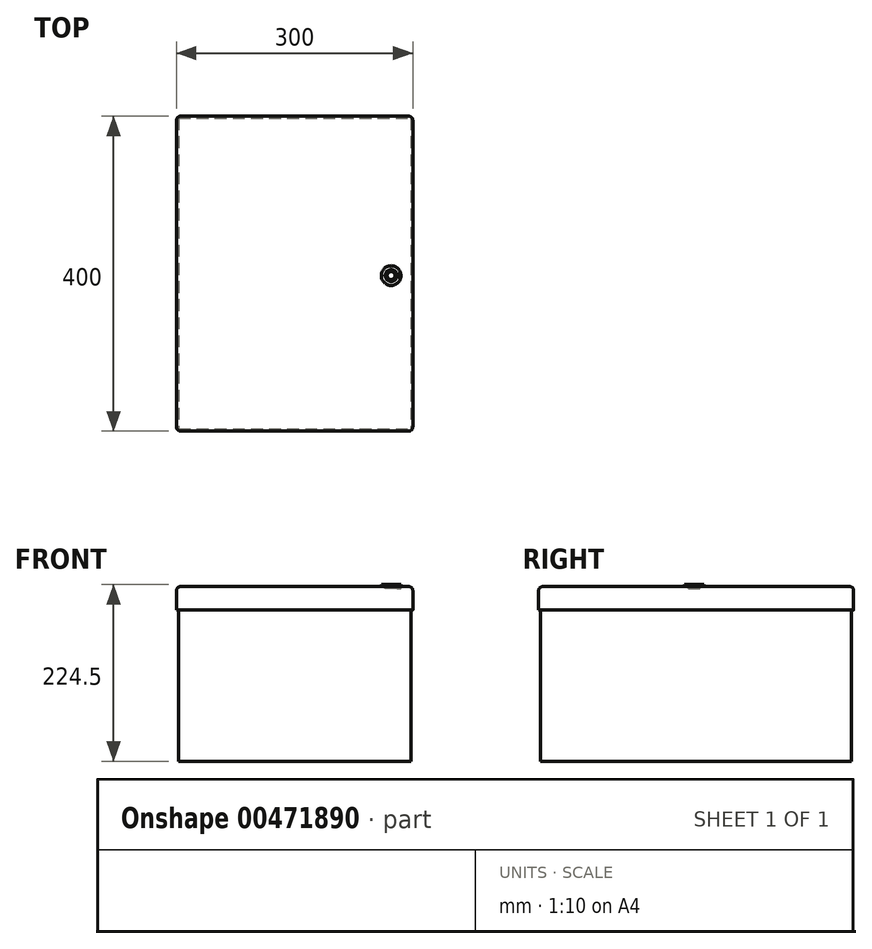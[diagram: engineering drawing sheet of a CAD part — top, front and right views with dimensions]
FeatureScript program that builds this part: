
annotation { "Feature Type Name" : "Feature", "Feature Type Description" : "" }
export const myFeature = defineFeature(function(context is Context, id is Id, definition is map)
    precondition{}
    {
        {
            var Q0;
            Q0=qCreatedBy(makeId("Top.planeOp"),FACE);
            var sketch = newSketch(context, id + "F0", { "sketchPlane" : qUnion([Q0])});
            skLineSegment(sketch, "E0.bottom", {"start": v(-145, 200) * mm, "end": v(150, 200) * mm});
            skLineSegment(sketch, "E0.top", {"start": v(-145, -195) * mm, "end": v(150, -195) * mm});
            skLineSegment(sketch, "E0.left", {"start": v(-145, 200) * mm, "end": v(-145, -195) * mm});
            skLineSegment(sketch, "E0.right", {"start": v(150, 200) * mm, "end": v(150, -195) * mm});
            skSolve(sketch);
        }
        {
            var Q0;
            Q0=makeQuery(id+"F0.imprint","IMPRINT",FACE,{"disambiguationData":[TD([[makeQuery(id+"F0.imprint","IMPRINT",EDGE,{"derivedFrom":sQuery(id+"F0.wireOp",EDGE,"E0.bottom")}),-1.0]])]});
            extrude(context, id + "F1", {"entities" : qUnion([Q0]), "endBound" : BoundingType.SYMMETRIC, "depth" : 220 * mm});
        }
        {
            var Q0;
            Q0=makeQuery(id+"F1.opExtrude","CAP_FACE",FACE,{"disambiguationData":[OSD([sQuery(id+"F0.wireOp",EDGE,"E0.bottom"),sQuery(id+"F0.wireOp",EDGE,"E0.top"),sQuery(id+"F0.wireOp",EDGE,"E0.left"),sQuery(id+"F0.wireOp",EDGE,"E0.right")])],"isStart":false});
            cPlane(context, id + "F2", {"entities" : qUnion([Q0]), "cplaneType" : CPlaneType.OFFSET, "offset" : 2 * mm, "width" : 150 * mm, "height" : 150 * mm});
        }
        {
            var Q0;
            Q0=qCreatedBy(id+"F2.planeOp",FACE);
            var sketch = newSketch(context, id + "F3", { "sketchPlane" : qUnion([Q0])});
            skLineSegment(sketch, "E1.bottom", {"start": v(-147.5, 202.5) * mm, "end": v(152.5, 202.5) * mm});
            skLineSegment(sketch, "E1.top", {"start": v(-147.5, -197.5) * mm, "end": v(152.5, -197.5) * mm});
            skLineSegment(sketch, "E1.left", {"start": v(-147.5, 202.5) * mm, "end": v(-147.5, -197.5) * mm});
            skLineSegment(sketch, "E1.right", {"start": v(152.5, 202.5) * mm, "end": v(152.5, -197.5) * mm});
            skSolve(sketch);
        }
        {
            var Q0;
            Q0=makeQuery(id+"F3.imprint","IMPRINT",FACE,{"disambiguationData":[TD([[makeQuery(id+"F3.imprint","IMPRINT",EDGE,{"derivedFrom":sQuery(id+"F3.wireOp",EDGE,"E1.bottom")}),-1.0]])]});
            extrude(context, id + "F4", {"entities" : qUnion([Q0]), "operationType" : NewBodyOperationType.ADD, "oppositeDirection" : true, "depth" : 30 * mm});
        }
        {
            var Q0;
            Q0=makeQuery(id+"F4.opExtrude","CAP_EDGE",EDGE,{"disambiguationData":[OSD([sQuery(id+"F3.wireOp",EDGE,"E1.right")])],"isStart":true});
            var Q1;
            Q1=makeQuery(id+"F4.opExtrude","CAP_EDGE",EDGE,{"disambiguationData":[OSD([sQuery(id+"F3.wireOp",EDGE,"E1.bottom")])],"isStart":true});
            var Q2;
            Q2=makeQuery(id+"F4.opExtrude","CAP_EDGE",EDGE,{"disambiguationData":[OSD([sQuery(id+"F3.wireOp",EDGE,"E1.left")])],"isStart":true});
            var Q3;
            Q3=makeQuery(id+"F4.opExtrude","CAP_EDGE",EDGE,{"disambiguationData":[OSD([sQuery(id+"F3.wireOp",EDGE,"E1.top")])],"isStart":true});
            var Q4;
            Q4=makeQuery(id+"F4.opExtrude","SWEPT_EDGE",EDGE,{"disambiguationData":[OSD([sQuery(id+"F3.wireOp",EDGE,"E1.bottom"),sQuery(id+"F3.wireOp",EDGE,"E1.right")])]});
            var Q5;
            Q5=makeQuery(id+"F4.opExtrude","SWEPT_EDGE",EDGE,{"disambiguationData":[OSD([sQuery(id+"F3.wireOp",EDGE,"E1.bottom"),sQuery(id+"F3.wireOp",EDGE,"E1.left")])]});
            var Q6;
            Q6=makeQuery(id+"F4.opExtrude","SWEPT_EDGE",EDGE,{"disambiguationData":[OSD([sQuery(id+"F3.wireOp",EDGE,"E1.top"),sQuery(id+"F3.wireOp",EDGE,"E1.right")])]});
            var Q7;
            Q7=makeQuery(id+"F4.opExtrude","SWEPT_EDGE",EDGE,{"disambiguationData":[OSD([sQuery(id+"F3.wireOp",EDGE,"E1.top"),sQuery(id+"F3.wireOp",EDGE,"E1.left")])]});
            fillet(context, id + "F5", {"entities" : qUnion([Q0, Q1, Q2, Q3, Q4, Q5, Q6, Q7]), "radius" : 5 * mm, "tangentPropagation" : true, "allowEdgeOverflow" : false});
        }
        {
            var Q0;
            Q0=makeQuery(id+"F4.opExtrude","CAP_FACE",FACE,{"disambiguationData":[OSD([sQuery(id+"F3.wireOp",EDGE,"E1.bottom"),sQuery(id+"F3.wireOp",EDGE,"E1.top"),sQuery(id+"F3.wireOp",EDGE,"E1.left"),sQuery(id+"F3.wireOp",EDGE,"E1.right")])],"isStart":true});
            var sketch = newSketch(context, id + "F6", { "sketchPlane" : qUnion([Q0])});
            skCircle(sketch, "E2", {"center": v(125, 0) * mm, "radius": 12.5 * mm});
            skArc(sketch, "E3", {"start": v(132.3, 1.7) * mm, "mid": v(117.5, 0) * mm, "end": v(132.3, -1.7) * mm});
            skLineSegment(sketch, "E4", {"start": v(112.5, 0) * mm, "end": v(113.08, -3.78) * mm});
            skLineSegment(sketch, "E5", {"start": v(132.3, 1.7) * mm, "end": v(137.38, 1.7) * mm});
            skLineSegment(sketch, "E6", {"start": v(137.38, -1.7) * mm, "end": v(132.3, -1.7) * mm});
            skCircle(sketch, "E7", {"center": v(125, 0) * mm, "radius": 5 * mm});
            skSolve(sketch);
        }
        {
            var Q0;
            Q0=makeQuery(id+"F6.imprint","IMPRINT",FACE,{"disambiguationData":[TD([[makeQuery(id+"F6.imprint","IMPRINT",EDGE,{"derivedFrom":sQuery(id+"F6.wireOp",EDGE,"E3")}),-1.0]])]});
            var Q1;
            Q1=makeQuery(id+"F6.imprint","IMPRINT",FACE,{"disambiguationData":[TD([[makeQuery(id+"F6.imprint","IMPRINT",EDGE,{"derivedFrom":sQuery(id+"F6.wireOp",EDGE,"E7")}),1.0]])]});
            extrude(context, id + "F7", {"entities" : qUnion([Q0, Q1]), "depth" : 2.5 * mm});
        }
        {
            var Q0;
            Q0=makeQuery(id+"F4.opExtrude","CAP_FACE",FACE,{"disambiguationData":[OSD([sQuery(id+"F3.wireOp",EDGE,"E1.bottom"),sQuery(id+"F3.wireOp",EDGE,"E1.top"),sQuery(id+"F3.wireOp",EDGE,"E1.left"),sQuery(id+"F3.wireOp",EDGE,"E1.right")])],"isStart":true});
            var sketch = newSketch(context, id + "F8", { "sketchPlane" : qUnion([Q0])});
            skLineSegment(sketch, "E8.0", {"start": v(132.3, 1.7) * mm, "end": v(137.38, 1.7) * mm});
            skLineSegment(sketch, "E9.0", {"start": v(137.38, -1.7) * mm, "end": v(132.3, -1.7) * mm});
            skArc(sketch, "E10.0", {"start": v(137.38, 1.7) * mm, "mid": v(124.15, 12.47) * mm, "end": v(112.5, 0) * mm});
            skArc(sketch, "E11.0", {"start": v(132.3, 1.7) * mm, "mid": v(117.5, 0) * mm, "end": v(132.3, -1.7) * mm});
            skLineSegment(sketch, "E12", {"start": v(137.38, 1.7) * mm, "end": v(137.38, -1.7) * mm});
            skCircle(sketch, "E13.0.0", {"center": v(125, 0) * mm, "radius": 5 * mm});
            skSolve(sketch);
        }
        {
            var Q0;
            Q0=makeQuery(id+"F8.imprint","IMPRINT",FACE,{"disambiguationData":[TD([[makeQuery(id+"F8.imprint","IMPRINT",EDGE,{"derivedFrom":sQuery(id+"F8.wireOp",EDGE,"E8.0")}),-1.0]])]});
            extrude(context, id + "F9", {"entities" : qUnion([Q0]), "operationType" : NewBodyOperationType.REMOVE, "oppositeDirection" : true, "depth" : 2.5 * mm});
        }
    });
